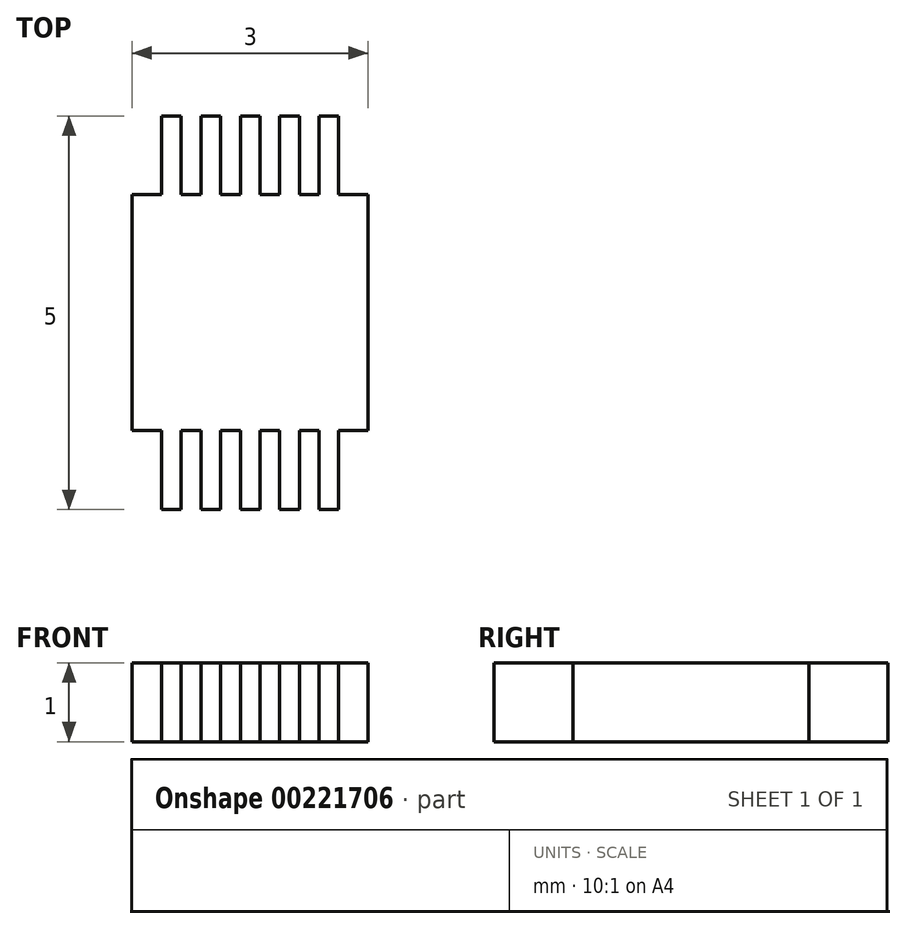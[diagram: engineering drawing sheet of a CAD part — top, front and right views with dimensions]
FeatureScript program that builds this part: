
annotation { "Feature Type Name" : "Feature", "Feature Type Description" : "" }
export const myFeature = defineFeature(function(context is Context, id is Id, definition is map)
    precondition{}
    {
        {
            var Q0;
            Q0=qCreatedBy(makeId("Top.planeOp"),FACE);
            var sketch = newSketch(context, id + "F0", { "sketchPlane" : qUnion([Q0])});
            skLineSegment(sketch, "E0.bottom", {"start": v(1.5, 1.5) * mm, "end": v(-1.5, 1.5) * mm});
            skLineSegment(sketch, "E0.top", {"start": v(1.5, -1.5) * mm, "end": v(-1.5, -1.5) * mm});
            skLineSegment(sketch, "E0.left", {"start": v(1.5, 1.5) * mm, "end": v(1.5, -1.5) * mm});
            skLineSegment(sketch, "E0.right", {"start": v(-1.5, 1.5) * mm, "end": v(-1.5, -1.5) * mm});
            skPoint(sketch, "E0.middle", {"position": v(0, 0) * mm});
            skLineSegment(sketch, "E1.bottom", {"start": v(-0.13, 1.5) * mm, "end": v(0.13, 1.5) * mm});
            skLineSegment(sketch, "E1.top", {"start": v(-0.12, 2.5) * mm, "end": v(0.12, 2.5) * mm});
            skLineSegment(sketch, "E1.left", {"start": v(-0.13, 1.5) * mm, "end": v(-0.12, 2.5) * mm});
            skLineSegment(sketch, "E1.right", {"start": v(0.12, 1.5) * mm, "end": v(0.12, 2.5) * mm});
            skLineSegment(sketch, "E2", {"start": v(0, 2.5) * mm, "end": v(0, 0) * mm, "construction": true});
            skLineSegment(sketch, "E3", {"start": v(0, 0) * mm, "end": v(1.5, 0) * mm, "construction": true});
            skLineSegment(sketch, "E4.bottom", {"start": v(-0.13, -1.5) * mm, "end": v(0.13, -1.5) * mm});
            skLineSegment(sketch, "E4.top", {"start": v(-0.12, -2.5) * mm, "end": v(0.12, -2.5) * mm});
            skLineSegment(sketch, "E4.left", {"start": v(-0.13, -1.5) * mm, "end": v(-0.13, -2.5) * mm});
            skLineSegment(sketch, "E4.right", {"start": v(0.12, -1.5) * mm, "end": v(0.12, -2.5) * mm});
            skLineSegment(sketch, "E5", {"start": v(0, -2.5) * mm, "end": v(0, 0) * mm, "construction": true});
            skLineSegment(sketch, "E6.bottom", {"start": v(-0.63, 2.5) * mm, "end": v(-0.37, 2.5) * mm});
            skLineSegment(sketch, "E6.top", {"start": v(-0.63, 1.5) * mm, "end": v(-0.37, 1.5) * mm});
            skLineSegment(sketch, "E6.left", {"start": v(-0.63, 2.5) * mm, "end": v(-0.63, 1.5) * mm});
            skLineSegment(sketch, "E6.right", {"start": v(-0.37, 2.5) * mm, "end": v(-0.37, 1.5) * mm});
            skLineSegment(sketch, "E7.bottom", {"start": v(-1.13, 2.5) * mm, "end": v(-0.87, 2.5) * mm});
            skLineSegment(sketch, "E7.top", {"start": v(-1.13, 1.5) * mm, "end": v(-0.87, 1.5) * mm});
            skLineSegment(sketch, "E7.left", {"start": v(-1.13, 2.5) * mm, "end": v(-1.13, 1.5) * mm});
            skLineSegment(sketch, "E7.right", {"start": v(-0.87, 2.5) * mm, "end": v(-0.87, 1.5) * mm});
            skLineSegment(sketch, "E8.bottom", {"start": v(0.37, 2.5) * mm, "end": v(0.63, 2.5) * mm});
            skLineSegment(sketch, "E8.top", {"start": v(0.37, 1.5) * mm, "end": v(0.63, 1.5) * mm});
            skLineSegment(sketch, "E8.left", {"start": v(0.37, 2.5) * mm, "end": v(0.37, 1.5) * mm});
            skLineSegment(sketch, "E8.right", {"start": v(0.63, 2.5) * mm, "end": v(0.63, 1.5) * mm});
            skLineSegment(sketch, "E9.bottom", {"start": v(0.87, 2.5) * mm, "end": v(1.13, 2.5) * mm});
            skLineSegment(sketch, "E9.top", {"start": v(0.87, 1.5) * mm, "end": v(1.13, 1.5) * mm});
            skLineSegment(sketch, "E9.left", {"start": v(0.87, 2.5) * mm, "end": v(0.87, 1.5) * mm});
            skLineSegment(sketch, "E9.right", {"start": v(1.13, 2.5) * mm, "end": v(1.13, 1.5) * mm});
            skLineSegment(sketch, "E10", {"start": v(-0.5, 2.5) * mm, "end": v(-0.5, 1.5) * mm, "construction": true});
            skLineSegment(sketch, "E11", {"start": v(-1, 2.5) * mm, "end": v(-1, 1.5) * mm, "construction": true});
            skLineSegment(sketch, "E12", {"start": v(0.5, 2.5) * mm, "end": v(0.5, 1.5) * mm, "construction": true});
            skLineSegment(sketch, "E13", {"start": v(1, 2.5) * mm, "end": v(1, 1.5) * mm, "construction": true});
            skLineSegment(sketch, "E14.bottom", {"start": v(-1.13, -1.5) * mm, "end": v(-0.87, -1.5) * mm});
            skLineSegment(sketch, "E14.top", {"start": v(-1.13, -2.5) * mm, "end": v(-0.87, -2.5) * mm});
            skLineSegment(sketch, "E14.left", {"start": v(-1.13, -1.5) * mm, "end": v(-1.13, -2.5) * mm});
            skLineSegment(sketch, "E14.right", {"start": v(-0.87, -1.5) * mm, "end": v(-0.87, -2.5) * mm});
            skLineSegment(sketch, "E15.bottom", {"start": v(-0.63, -1.5) * mm, "end": v(-0.37, -1.5) * mm});
            skLineSegment(sketch, "E15.top", {"start": v(-0.63, -2.5) * mm, "end": v(-0.37, -2.5) * mm});
            skLineSegment(sketch, "E15.left", {"start": v(-0.63, -1.5) * mm, "end": v(-0.63, -2.5) * mm});
            skLineSegment(sketch, "E15.right", {"start": v(-0.37, -1.5) * mm, "end": v(-0.37, -2.5) * mm});
            skLineSegment(sketch, "E16.bottom", {"start": v(0.37, -1.5) * mm, "end": v(0.63, -1.5) * mm});
            skLineSegment(sketch, "E16.top", {"start": v(0.37, -2.5) * mm, "end": v(0.63, -2.5) * mm});
            skLineSegment(sketch, "E16.left", {"start": v(0.37, -1.5) * mm, "end": v(0.37, -2.5) * mm});
            skLineSegment(sketch, "E16.right", {"start": v(0.63, -1.5) * mm, "end": v(0.63, -2.5) * mm});
            skLineSegment(sketch, "E17.bottom", {"start": v(0.87, -1.5) * mm, "end": v(1.13, -1.5) * mm});
            skLineSegment(sketch, "E17.top", {"start": v(0.87, -2.5) * mm, "end": v(1.13, -2.5) * mm});
            skLineSegment(sketch, "E17.left", {"start": v(0.87, -1.5) * mm, "end": v(0.87, -2.5) * mm});
            skLineSegment(sketch, "E17.right", {"start": v(1.13, -1.5) * mm, "end": v(1.13, -2.5) * mm});
            skLineSegment(sketch, "E18", {"start": v(-1, -1.5) * mm, "end": v(-1, -2.5) * mm, "construction": true});
            skLineSegment(sketch, "E19", {"start": v(-0.5, -1.5) * mm, "end": v(-0.5, -2.5) * mm, "construction": true});
            skLineSegment(sketch, "E20", {"start": v(0.5, -2.5) * mm, "end": v(0.5, -1.5) * mm, "construction": true});
            skLineSegment(sketch, "E21", {"start": v(1, -2.5) * mm, "end": v(1, -1.5) * mm, "construction": true});
            skLineSegment(sketch, "E22", {"start": v(-1, -1.5) * mm, "end": v(0, 0) * mm, "construction": true});
            skLineSegment(sketch, "E23", {"start": v(1, -1.5) * mm, "end": v(0, 0) * mm, "construction": true});
            skLineSegment(sketch, "E24", {"start": v(-0.5, -1.5) * mm, "end": v(0, 0) * mm, "construction": true});
            skLineSegment(sketch, "E25", {"start": v(0.5, -1.5) * mm, "end": v(0, 0) * mm, "construction": true});
            skSolve(sketch);
        }
        {
            var Q0;
            Q0 = qSketchRegion(id + "F0", true);
            extrude(context, id + "F1", {"entities" : qUnion([Q0]), "depth" : 1 * mm});
        }
    });
